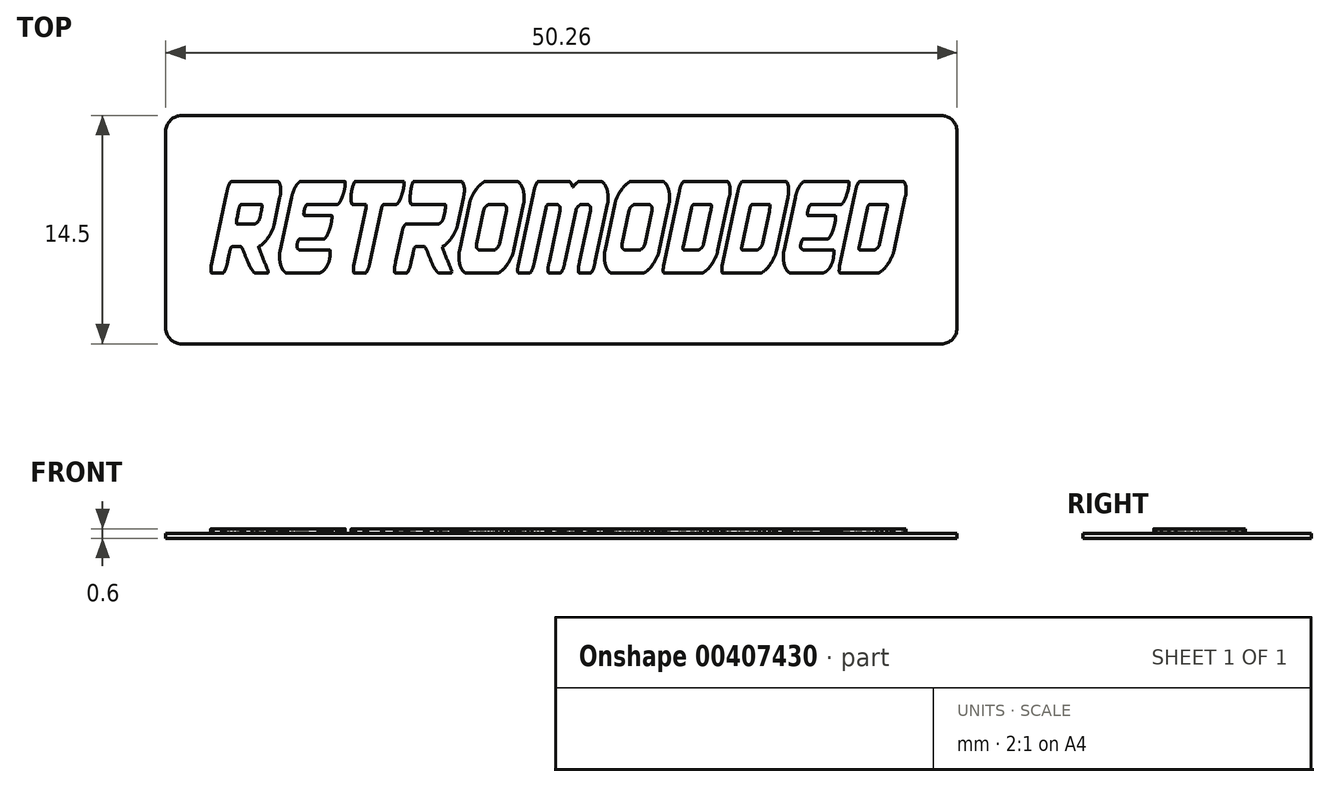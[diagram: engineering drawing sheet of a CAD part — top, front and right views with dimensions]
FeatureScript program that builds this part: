
annotation { "Feature Type Name" : "Feature", "Feature Type Description" : "" }
export const myFeature = defineFeature(function(context is Context, id is Id, definition is map)
    precondition{}
    {
        {
            var Q0;
            Q0=qCreatedBy(makeId("Top.planeOp"),FACE);
            var sketch = newSketch(context, id + "F0", { "sketchPlane" : qUnion([Q0])});
            skLineSegment(sketch, "E0.bottom", {"start": v(-24.13, 0) * mm, "end": v(24.13, 0) * mm});
            skLineSegment(sketch, "E0.top", {"start": v(-24.13, -14.5) * mm, "end": v(24.13, -14.5) * mm});
            skLineSegment(sketch, "E0.left", {"start": v(-25.12, -1) * mm, "end": v(-25.12, -13.5) * mm});
            skLineSegment(sketch, "E0.right", {"start": v(25.12, -1) * mm, "end": v(25.12, -13.5) * mm});
            skPoint(sketch, "E1.visualSharp", {"position": v(-25.13, 0) * mm});
            skArc(sketch, "E1.filletArc", {"start": v(-24.13, 0) * mm, "mid": v(-24.83, -0.3) * mm, "end": v(-25.13, -1) * mm});
            skPoint(sketch, "E2.visualSharp", {"position": v(-25.13, -14.5) * mm});
            skArc(sketch, "E2.filletArc", {"start": v(-25.13, -13.5) * mm, "mid": v(-24.83, -14.2) * mm, "end": v(-24.13, -14.5) * mm});
            skPoint(sketch, "E3.visualSharp", {"position": v(25.12, 0) * mm});
            skArc(sketch, "E3.filletArc", {"start": v(25.13, -1) * mm, "mid": v(24.83, -0.3) * mm, "end": v(24.13, 0) * mm});
            skPoint(sketch, "E4.visualSharp", {"position": v(25.12, -14.5) * mm});
            skArc(sketch, "E4.filletArc", {"start": v(24.13, -14.5) * mm, "mid": v(24.83, -14.2) * mm, "end": v(25.13, -13.5) * mm});
            skSolve(sketch);
        }
        {
            var Q0;
            Q0=qCreatedBy(makeId("Top.planeOp"),FACE);
            var sketch = newSketch(context, id + "F1", { "sketchPlane" : qUnion([Q0])});
            skLineSegment(sketch, "E5", {"start": v(-20.61, -6.53) * mm, "end": v(-20.5, -6.01) * mm});
            skFitSpline(sketch, "E6", {"points": [v(-20.5, -6.01) * mm, v(-20.48, -5.91) * mm, v(-20.45, -5.83) * mm, v(-20.42, -5.76) * mm]});
            skFitSpline(sketch, "E7", {"points": [v(-20.42, -5.76) * mm, v(-20.4, -5.69) * mm, v(-20.36, -5.65) * mm, v(-20.33, -5.64) * mm]});
            skLineSegment(sketch, "E8", {"start": v(-20.33, -5.64) * mm, "end": v(-19.09, -5.64) * mm});
            skFitSpline(sketch, "E9", {"points": [v(-19.09, -5.64) * mm, v(-19.04, -5.64) * mm, v(-19.02, -5.69) * mm, v(-19.02, -5.79) * mm]});
            skFitSpline(sketch, "E10", {"points": [v(-19.02, -5.79) * mm, v(-19.02, -5.83) * mm, v(-19.02, -5.88) * mm, v(-19.04, -5.95) * mm]});
            skFitSpline(sketch, "E11", {"points": [v(-19.04, -5.95) * mm, v(-19.04, -6) * mm, v(-19.05, -6.05) * mm, v(-19.06, -6.1) * mm]});
            skLineSegment(sketch, "E12", {"start": v(-19.06, -6.1) * mm, "end": v(-19.14, -6.49) * mm});
            skFitSpline(sketch, "E13", {"points": [v(-19.14, -6.49) * mm, v(-19.2, -6.62) * mm, v(-19.25, -6.72) * mm, v(-19.32, -6.79) * mm]});
            skFitSpline(sketch, "E14", {"points": [v(-19.32, -6.79) * mm, v(-19.4, -6.85) * mm, v(-19.46, -6.88) * mm, v(-19.53, -6.88) * mm]});
            skLineSegment(sketch, "E15", {"start": v(-19.53, -6.88) * mm, "end": v(-20.6, -6.88) * mm});
            skFitSpline(sketch, "E16", {"points": [v(-20.6, -6.88) * mm, v(-20.62, -6.88) * mm, v(-20.63, -6.83) * mm, v(-20.63, -6.74) * mm]});
            skFitSpline(sketch, "E17", {"points": [v(-20.63, -6.74) * mm, v(-20.63, -6.72) * mm, v(-20.63, -6.7) * mm, v(-20.63, -6.66) * mm]});
            skFitSpline(sketch, "E18", {"points": [v(-20.63, -6.66) * mm, v(-20.62, -6.62) * mm, v(-20.62, -6.58) * mm, v(-20.61, -6.53) * mm]});
            skLineSegment(sketch, "E19", {"start": v(-18.08, -4.18) * mm, "end": v(-20.86, -4.18) * mm});
            skFitSpline(sketch, "E20", {"points": [v(-20.86, -4.18) * mm, v(-20.96, -4.18) * mm, v(-21.03, -4.24) * mm, v(-21.09, -4.35) * mm]});
            skFitSpline(sketch, "E21", {"points": [v(-21.09, -4.35) * mm, v(-21.14, -4.46) * mm, v(-21.2, -4.64) * mm, v(-21.25, -4.9) * mm]});
            skLineSegment(sketch, "E22", {"start": v(-21.25, -4.9) * mm, "end": v(-22.19, -9.28) * mm});
            skFitSpline(sketch, "E23", {"points": [v(-22.19, -9.28) * mm, v(-22.2, -9.38) * mm, v(-22.22, -9.47) * mm, v(-22.24, -9.55) * mm]});
            skFitSpline(sketch, "E24", {"points": [v(-22.24, -9.55) * mm, v(-22.25, -9.63) * mm, v(-22.26, -9.7) * mm, v(-22.26, -9.76) * mm]});
            skFitSpline(sketch, "E25", {"points": [v(-22.26, -9.76) * mm, v(-22.26, -9.92) * mm, v(-22.2, -10) * mm, v(-22.1, -10) * mm]});
            skLineSegment(sketch, "E26", {"start": v(-22.1, -10) * mm, "end": v(-21.6, -10) * mm});
            skFitSpline(sketch, "E27", {"points": [v(-21.6, -10) * mm, v(-21.5, -10) * mm, v(-21.42, -9.94) * mm, v(-21.37, -9.82) * mm]});
            skFitSpline(sketch, "E28", {"points": [v(-21.37, -9.82) * mm, v(-21.3, -9.7) * mm, v(-21.25, -9.52) * mm, v(-21.2, -9.28) * mm]});
            skLineSegment(sketch, "E29", {"start": v(-21.2, -9.28) * mm, "end": v(-21.1, -8.79) * mm});
            skFitSpline(sketch, "E30", {"points": [v(-21.1, -8.79) * mm, v(-21.03, -8.5) * mm, v(-20.96, -8.35) * mm, v(-20.88, -8.33) * mm]});
            skLineSegment(sketch, "E31", {"start": v(-20.88, -8.33) * mm, "end": v(-20.35, -8.33) * mm});
            skFitSpline(sketch, "E32", {"points": [v(-20.35, -8.33) * mm, v(-20.27, -8.44) * mm, v(-20.2, -8.58) * mm, v(-20.13, -8.77) * mm]});
            skFitSpline(sketch, "E33", {"points": [v(-20.13, -8.77) * mm, v(-20.05, -8.96) * mm, v(-19.98, -9.14) * mm, v(-19.9, -9.33) * mm]});
            skFitSpline(sketch, "E34", {"points": [v(-19.9, -9.33) * mm, v(-19.82, -9.5) * mm, v(-19.73, -9.67) * mm, v(-19.64, -9.8) * mm]});
            skFitSpline(sketch, "E35", {"points": [v(-19.64, -9.8) * mm, v(-19.55, -9.93) * mm, v(-19.44, -10) * mm, v(-19.32, -10) * mm]});
            skLineSegment(sketch, "E36", {"start": v(-19.32, -10) * mm, "end": v(-18.66, -10) * mm});
            skFitSpline(sketch, "E37", {"points": [v(-18.66, -10) * mm, v(-18.65, -10) * mm, v(-18.64, -9.98) * mm, v(-18.62, -9.94) * mm]});
            skLineSegment(sketch, "E38", {"start": v(-18.62, -9.94) * mm, "end": v(-18.62, -9.9) * mm});
            skFitSpline(sketch, "E39", {"points": [v(-18.62, -9.9) * mm, v(-18.72, -9.63) * mm, v(-18.82, -9.37) * mm, v(-18.93, -9.13) * mm]});
            skFitSpline(sketch, "E40", {"points": [v(-18.93, -9.13) * mm, v(-19.03, -8.87) * mm, v(-19.13, -8.6) * mm, v(-19.24, -8.31) * mm]});
            skFitSpline(sketch, "E41", {"points": [v(-19.24, -8.31) * mm, v(-19.14, -8.28) * mm, v(-19.04, -8.22) * mm, v(-18.94, -8.12) * mm]});
            skFitSpline(sketch, "E42", {"points": [v(-18.94, -8.12) * mm, v(-18.84, -8.02) * mm, v(-18.74, -7.9) * mm, v(-18.65, -7.78) * mm]});
            skFitSpline(sketch, "E43", {"points": [v(-18.65, -7.78) * mm, v(-18.55, -7.64) * mm, v(-18.47, -7.5) * mm, v(-18.4, -7.35) * mm]});
            skFitSpline(sketch, "E44", {"points": [v(-18.4, -7.35) * mm, v(-18.33, -7.2) * mm, v(-18.28, -7.07) * mm, v(-18.25, -6.94) * mm]});
            skLineSegment(sketch, "E45", {"start": v(-18.25, -6.94) * mm, "end": v(-17.89, -5.2) * mm});
            skFitSpline(sketch, "E46", {"points": [v(-17.89, -5.2) * mm, v(-17.85, -5.04) * mm, v(-17.83, -4.88) * mm, v(-17.83, -4.73) * mm]});
            skFitSpline(sketch, "E47", {"points": [v(-17.83, -4.73) * mm, v(-17.83, -4.57) * mm, v(-17.85, -4.45) * mm, v(-17.9, -4.34) * mm]});
            skFitSpline(sketch, "E48", {"points": [v(-17.9, -4.34) * mm, v(-17.93, -4.24) * mm, v(-18, -4.18) * mm, v(-18.08, -4.18) * mm]});
            skFitSpline(sketch, "E49", {"points": [v(-17.86, -8.6) * mm, v(-17.89, -8.69) * mm, v(-17.9, -8.8) * mm, v(-17.9, -8.94) * mm]});
            skFitSpline(sketch, "E50", {"points": [v(-17.9, -8.94) * mm, v(-17.9, -9.07) * mm, v(-17.89, -9.2) * mm, v(-17.86, -9.32) * mm]});
            skFitSpline(sketch, "E51", {"points": [v(-17.86, -9.32) * mm, v(-17.84, -9.44) * mm, v(-17.8, -9.56) * mm, v(-17.76, -9.66) * mm]});
            skFitSpline(sketch, "E52", {"points": [v(-17.76, -9.66) * mm, v(-17.71, -9.76) * mm, v(-17.66, -9.84) * mm, v(-17.6, -9.9) * mm]});
            skFitSpline(sketch, "E53", {"points": [v(-17.6, -9.9) * mm, v(-17.53, -9.97) * mm, v(-17.46, -10) * mm, v(-17.38, -10) * mm]});
            skLineSegment(sketch, "E54", {"start": v(-17.38, -10) * mm, "end": v(-15.47, -10) * mm});
            skFitSpline(sketch, "E55", {"points": [v(-15.47, -10) * mm, v(-15.4, -10) * mm, v(-15.32, -9.98) * mm, v(-15.24, -9.94) * mm]});
            skFitSpline(sketch, "E56", {"points": [v(-15.24, -9.94) * mm, v(-15.16, -9.9) * mm, v(-15.1, -9.83) * mm, v(-15.02, -9.75) * mm]});
            skFitSpline(sketch, "E57", {"points": [v(-15.02, -9.75) * mm, v(-14.96, -9.67) * mm, v(-14.9, -9.58) * mm, v(-14.85, -9.47) * mm]});
            skFitSpline(sketch, "E58", {"points": [v(-14.85, -9.47) * mm, v(-14.8, -9.36) * mm, v(-14.75, -9.24) * mm, v(-14.72, -9.1) * mm]});
            skFitSpline(sketch, "E59", {"points": [v(-14.72, -9.1) * mm, v(-14.71, -9.07) * mm, v(-14.7, -9.02) * mm, v(-14.7, -8.93) * mm]});
            skFitSpline(sketch, "E60", {"points": [v(-14.7, -8.93) * mm, v(-14.69, -8.84) * mm, v(-14.68, -8.76) * mm, v(-14.68, -8.68) * mm]});
            skFitSpline(sketch, "E61", {"points": [v(-14.68, -8.68) * mm, v(-14.68, -8.59) * mm, v(-14.7, -8.54) * mm, v(-14.72, -8.54) * mm]});
            skLineSegment(sketch, "E62", {"start": v(-14.72, -8.54) * mm, "end": v(-16.55, -8.54) * mm});
            skFitSpline(sketch, "E63", {"points": [v(-16.55, -8.54) * mm, v(-16.6, -8.54) * mm, v(-16.66, -8.52) * mm, v(-16.72, -8.47) * mm]});
            skFitSpline(sketch, "E64", {"points": [v(-16.72, -8.47) * mm, v(-16.77, -8.43) * mm, v(-16.8, -8.35) * mm, v(-16.8, -8.25) * mm]});
            skFitSpline(sketch, "E65", {"points": [v(-16.8, -8.25) * mm, v(-16.8, -8.25) * mm, v(-16.8, -8.24) * mm, v(-16.8, -8.23) * mm]});
            skFitSpline(sketch, "E66", {"points": [v(-16.8, -8.23) * mm, v(-16.79, -8.2) * mm, v(-16.79, -8.19) * mm, v(-16.78, -8.16) * mm]});
            skFitSpline(sketch, "E67", {"points": [v(-16.78, -8.16) * mm, v(-16.75, -8.05) * mm, v(-16.72, -7.96) * mm, v(-16.7, -7.91) * mm]});
            skFitSpline(sketch, "E68", {"points": [v(-16.7, -7.91) * mm, v(-16.67, -7.86) * mm, v(-16.63, -7.83) * mm, v(-16.58, -7.83) * mm]});
            skLineSegment(sketch, "E69", {"start": v(-16.58, -7.83) * mm, "end": v(-15.1, -7.83) * mm});
            skFitSpline(sketch, "E70", {"points": [v(-15.1, -7.83) * mm, v(-15.05, -7.83) * mm, v(-15, -7.8) * mm, v(-14.96, -7.74) * mm]});
            skFitSpline(sketch, "E71", {"points": [v(-14.96, -7.74) * mm, v(-14.92, -7.67) * mm, v(-14.87, -7.6) * mm, v(-14.83, -7.5) * mm]});
            skFitSpline(sketch, "E72", {"points": [v(-14.83, -7.5) * mm, v(-14.79, -7.4) * mm, v(-14.75, -7.3) * mm, v(-14.71, -7.18) * mm]});
            skFitSpline(sketch, "E73", {"points": [v(-14.71, -7.18) * mm, v(-14.68, -7.07) * mm, v(-14.65, -6.96) * mm, v(-14.62, -6.86) * mm]});
            skFitSpline(sketch, "E74", {"points": [v(-14.62, -6.86) * mm, v(-14.61, -6.83) * mm, v(-14.6, -6.77) * mm, v(-14.6, -6.7) * mm]});
            skFitSpline(sketch, "E75", {"points": [v(-14.6, -6.7) * mm, v(-14.58, -6.6) * mm, v(-14.58, -6.53) * mm, v(-14.58, -6.47) * mm]});
            skFitSpline(sketch, "E76", {"points": [v(-14.58, -6.47) * mm, v(-14.58, -6.4) * mm, v(-14.59, -6.35) * mm, v(-14.61, -6.35) * mm]});
            skLineSegment(sketch, "E77", {"start": v(-14.61, -6.35) * mm, "end": v(-16.3, -6.35) * mm});
            skFitSpline(sketch, "E78", {"points": [v(-16.3, -6.35) * mm, v(-16.32, -6.35) * mm, v(-16.34, -6.34) * mm, v(-16.35, -6.31) * mm]});
            skFitSpline(sketch, "E79", {"points": [v(-16.35, -6.31) * mm, v(-16.35, -6.28) * mm, v(-16.36, -6.25) * mm, v(-16.36, -6.22) * mm]});
            skFitSpline(sketch, "E80", {"points": [v(-16.36, -6.22) * mm, v(-16.36, -6.2) * mm, v(-16.36, -6.2) * mm, v(-16.36, -6.18) * mm]});
            skFitSpline(sketch, "E81", {"points": [v(-16.36, -6.18) * mm, v(-16.35, -6.16) * mm, v(-16.35, -6.14) * mm, v(-16.35, -6.1) * mm]});
            skFitSpline(sketch, "E82", {"points": [v(-16.35, -6.1) * mm, v(-16.34, -6.06) * mm, v(-16.33, -6.01) * mm, v(-16.32, -5.96) * mm]});
            skFitSpline(sketch, "E83", {"points": [v(-16.32, -5.96) * mm, v(-16.3, -5.9) * mm, v(-16.28, -5.86) * mm, v(-16.26, -5.81) * mm]});
            skFitSpline(sketch, "E84", {"points": [v(-16.26, -5.81) * mm, v(-16.24, -5.76) * mm, v(-16.22, -5.72) * mm, v(-16.2, -5.7) * mm]});
            skFitSpline(sketch, "E85", {"points": [v(-16.2, -5.7) * mm, v(-16.17, -5.66) * mm, v(-16.15, -5.64) * mm, v(-16.12, -5.64) * mm]});
            skLineSegment(sketch, "E86", {"start": v(-16.12, -5.64) * mm, "end": v(-14.26, -5.64) * mm});
            skFitSpline(sketch, "E87", {"points": [v(-14.26, -5.64) * mm, v(-14.22, -5.64) * mm, v(-14.17, -5.61) * mm, v(-14.12, -5.56) * mm]});
            skFitSpline(sketch, "E88", {"points": [v(-14.12, -5.56) * mm, v(-14.07, -5.5) * mm, v(-14.03, -5.42) * mm, v(-13.99, -5.33) * mm]});
            skFitSpline(sketch, "E89", {"points": [v(-13.99, -5.33) * mm, v(-13.94, -5.23) * mm, v(-13.9, -5.13) * mm, v(-13.87, -5.01) * mm]});
            skFitSpline(sketch, "E90", {"points": [v(-13.87, -5.01) * mm, v(-13.83, -4.9) * mm, v(-13.8, -4.8) * mm, v(-13.77, -4.7) * mm]});
            skFitSpline(sketch, "E91", {"points": [v(-13.77, -4.7) * mm, v(-13.76, -4.66) * mm, v(-13.76, -4.6) * mm, v(-13.74, -4.52) * mm]});
            skFitSpline(sketch, "E92", {"points": [v(-13.74, -4.52) * mm, v(-13.73, -4.44) * mm, v(-13.73, -4.36) * mm, v(-13.73, -4.3) * mm]});
            skFitSpline(sketch, "E93", {"points": [v(-13.73, -4.3) * mm, v(-13.73, -4.22) * mm, v(-13.74, -4.18) * mm, v(-13.77, -4.18) * mm]});
            skLineSegment(sketch, "E94", {"start": v(-13.77, -4.18) * mm, "end": v(-16.5, -4.18) * mm});
            skFitSpline(sketch, "E95", {"points": [v(-16.5, -4.18) * mm, v(-16.57, -4.18) * mm, v(-16.64, -4.21) * mm, v(-16.7, -4.28) * mm]});
            skFitSpline(sketch, "E96", {"points": [v(-16.7, -4.28) * mm, v(-16.76, -4.33) * mm, v(-16.82, -4.4) * mm, v(-16.88, -4.5) * mm]});
            skFitSpline(sketch, "E97", {"points": [v(-16.88, -4.5) * mm, v(-16.93, -4.6) * mm, v(-16.98, -4.71) * mm, v(-17.03, -4.84) * mm]});
            skFitSpline(sketch, "E98", {"points": [v(-17.03, -4.84) * mm, v(-17.07, -4.96) * mm, v(-17.1, -5.08) * mm, v(-17.14, -5.2) * mm]});
            skLineSegment(sketch, "E99", {"start": v(-17.14, -5.2) * mm, "end": v(-17.86, -8.6) * mm});
            skFitSpline(sketch, "E100", {"points": [v(-13.14, -9.28) * mm, v(-13.16, -9.38) * mm, v(-13.17, -9.47) * mm, v(-13.19, -9.55) * mm]});
            skFitSpline(sketch, "E101", {"points": [v(-13.19, -9.55) * mm, v(-13.2, -9.63) * mm, v(-13.2, -9.7) * mm, v(-13.2, -9.76) * mm]});
            skFitSpline(sketch, "E102", {"points": [v(-13.2, -9.76) * mm, v(-13.2, -9.92) * mm, v(-13.16, -10) * mm, v(-13.06, -10) * mm]});
            skLineSegment(sketch, "E103", {"start": v(-13.06, -10) * mm, "end": v(-12.54, -10) * mm});
            skFitSpline(sketch, "E104", {"points": [v(-12.54, -10) * mm, v(-12.45, -10) * mm, v(-12.37, -9.94) * mm, v(-12.32, -9.82) * mm]});
            skFitSpline(sketch, "E105", {"points": [v(-12.32, -9.82) * mm, v(-12.26, -9.7) * mm, v(-12.2, -9.52) * mm, v(-12.15, -9.28) * mm]});
            skLineSegment(sketch, "E106", {"start": v(-12.15, -9.28) * mm, "end": v(-11.43, -5.89) * mm});
            skFitSpline(sketch, "E107", {"points": [v(-11.43, -5.89) * mm, v(-11.4, -5.82) * mm, v(-11.38, -5.77) * mm, v(-11.35, -5.72) * mm]});
            skFitSpline(sketch, "E108", {"points": [v(-11.35, -5.72) * mm, v(-11.32, -5.67) * mm, v(-11.3, -5.64) * mm, v(-11.28, -5.64) * mm]});
            skLineSegment(sketch, "E109", {"start": v(-11.28, -5.64) * mm, "end": v(-10.52, -5.64) * mm});
            skFitSpline(sketch, "E110", {"points": [v(-10.52, -5.64) * mm, v(-10.48, -5.64) * mm, v(-10.43, -5.61) * mm, v(-10.38, -5.56) * mm]});
            skFitSpline(sketch, "E111", {"points": [v(-10.38, -5.56) * mm, v(-10.33, -5.5) * mm, v(-10.29, -5.42) * mm, v(-10.25, -5.33) * mm]});
            skFitSpline(sketch, "E112", {"points": [v(-10.25, -5.33) * mm, v(-10.2, -5.23) * mm, v(-10.16, -5.13) * mm, v(-10.13, -5.01) * mm]});
            skFitSpline(sketch, "E113", {"points": [v(-10.13, -5.01) * mm, v(-10.1, -4.9) * mm, v(-10.06, -4.8) * mm, v(-10.04, -4.7) * mm]});
            skFitSpline(sketch, "E114", {"points": [v(-10.04, -4.7) * mm, v(-10.03, -4.66) * mm, v(-10.02, -4.6) * mm, v(-10, -4.52) * mm]});
            skFitSpline(sketch, "E115", {"points": [v(-10, -4.52) * mm, v(-10, -4.44) * mm, v(-10, -4.36) * mm, v(-10, -4.3) * mm]});
            skFitSpline(sketch, "E116", {"points": [v(-10, -4.3) * mm, v(-10, -4.22) * mm, v(-10, -4.18) * mm, v(-10.03, -4.18) * mm]});
            skLineSegment(sketch, "E117", {"start": v(-10.03, -4.18) * mm, "end": v(-13.08, -4.18) * mm});
            skFitSpline(sketch, "E118", {"points": [v(-13.08, -4.18) * mm, v(-13.1, -4.18) * mm, v(-13.12, -4.2) * mm, v(-13.15, -4.25) * mm]});
            skFitSpline(sketch, "E119", {"points": [v(-13.15, -4.25) * mm, v(-13.17, -4.3) * mm, v(-13.2, -4.34) * mm, v(-13.21, -4.4) * mm]});
            skFitSpline(sketch, "E120", {"points": [v(-13.21, -4.4) * mm, v(-13.23, -4.45) * mm, v(-13.25, -4.5) * mm, v(-13.27, -4.56) * mm]});
            skFitSpline(sketch, "E121", {"points": [v(-13.27, -4.56) * mm, v(-13.28, -4.61) * mm, v(-13.3, -4.66) * mm, v(-13.3, -4.68) * mm]});
            skFitSpline(sketch, "E122", {"points": [v(-13.3, -4.68) * mm, v(-13.32, -4.78) * mm, v(-13.34, -4.88) * mm, v(-13.34, -4.97) * mm]});
            skFitSpline(sketch, "E123", {"points": [v(-13.34, -4.97) * mm, v(-13.35, -5.06) * mm, v(-13.35, -5.15) * mm, v(-13.35, -5.24) * mm]});
            skFitSpline(sketch, "E124", {"points": [v(-13.35, -5.24) * mm, v(-13.35, -5.36) * mm, v(-13.35, -5.45) * mm, v(-13.33, -5.53) * mm]});
            skFitSpline(sketch, "E125", {"points": [v(-13.33, -5.53) * mm, v(-13.3, -5.6) * mm, v(-13.27, -5.64) * mm, v(-13.21, -5.64) * mm]});
            skLineSegment(sketch, "E126", {"start": v(-13.21, -5.64) * mm, "end": v(-12.46, -5.64) * mm});
            skFitSpline(sketch, "E127", {"points": [v(-12.46, -5.64) * mm, v(-12.42, -5.64) * mm, v(-12.4, -5.7) * mm, v(-12.4, -5.8) * mm]});
            skFitSpline(sketch, "E128", {"points": [v(-12.4, -5.8) * mm, v(-12.4, -5.8) * mm, v(-12.4, -5.81) * mm, v(-12.41, -5.83) * mm]});
            skFitSpline(sketch, "E129", {"points": [v(-12.41, -5.83) * mm, v(-12.41, -5.84) * mm, v(-12.41, -5.86) * mm, v(-12.42, -5.89) * mm]});
            skLineSegment(sketch, "E130", {"start": v(-12.42, -5.89) * mm, "end": v(-13.14, -9.28) * mm});
            skLineSegment(sketch, "E131", {"start": v(-13.14, -9.28) * mm, "end": v(-13.14, -9.28) * mm});
            skLineSegment(sketch, "E132", {"start": v(-7.43, -5.64) * mm, "end": v(-9.47, -5.64) * mm});
            skFitSpline(sketch, "E133", {"points": [v(-9.47, -5.64) * mm, v(-9.52, -5.64) * mm, v(-9.56, -5.6) * mm, v(-9.58, -5.53) * mm]});
            skFitSpline(sketch, "E134", {"points": [v(-9.58, -5.53) * mm, v(-9.6, -5.45) * mm, v(-9.6, -5.36) * mm, v(-9.6, -5.24) * mm]});
            skFitSpline(sketch, "E135", {"points": [v(-9.6, -5.24) * mm, v(-9.6, -5.2) * mm, v(-9.6, -5.1) * mm, v(-9.6, -5) * mm]});
            skFitSpline(sketch, "E136", {"points": [v(-9.6, -5) * mm, v(-9.58, -4.88) * mm, v(-9.56, -4.76) * mm, v(-9.54, -4.64) * mm]});
            skFitSpline(sketch, "E137", {"points": [v(-9.54, -4.64) * mm, v(-9.52, -4.52) * mm, v(-9.5, -4.42) * mm, v(-9.46, -4.33) * mm]});
            skFitSpline(sketch, "E138", {"points": [v(-9.46, -4.33) * mm, v(-9.43, -4.23) * mm, v(-9.39, -4.18) * mm, v(-9.34, -4.18) * mm]});
            skLineSegment(sketch, "E139", {"start": v(-9.34, -4.18) * mm, "end": v(-6.42, -4.18) * mm});
            skFitSpline(sketch, "E140", {"points": [v(-6.42, -4.18) * mm, v(-6.33, -4.18) * mm, v(-6.27, -4.24) * mm, v(-6.23, -4.34) * mm]});
            skFitSpline(sketch, "E141", {"points": [v(-6.23, -4.34) * mm, v(-6.19, -4.45) * mm, v(-6.16, -4.57) * mm, v(-6.16, -4.73) * mm]});
            skFitSpline(sketch, "E142", {"points": [v(-6.16, -4.73) * mm, v(-6.16, -4.88) * mm, v(-6.18, -5.04) * mm, v(-6.22, -5.2) * mm]});
            skLineSegment(sketch, "E143", {"start": v(-6.22, -5.2) * mm, "end": v(-6.59, -6.94) * mm});
            skFitSpline(sketch, "E144", {"points": [v(-6.59, -6.94) * mm, v(-6.62, -7.07) * mm, v(-6.67, -7.2) * mm, v(-6.74, -7.35) * mm]});
            skFitSpline(sketch, "E145", {"points": [v(-6.74, -7.35) * mm, v(-6.8, -7.5) * mm, v(-6.89, -7.64) * mm, v(-6.98, -7.78) * mm]});
            skFitSpline(sketch, "E146", {"points": [v(-6.98, -7.78) * mm, v(-7.07, -7.9) * mm, v(-7.17, -8.02) * mm, v(-7.28, -8.12) * mm]});
            skFitSpline(sketch, "E147", {"points": [v(-7.28, -8.12) * mm, v(-7.38, -8.22) * mm, v(-7.48, -8.28) * mm, v(-7.57, -8.31) * mm]});
            skFitSpline(sketch, "E148", {"points": [v(-7.57, -8.31) * mm, v(-7.47, -8.6) * mm, v(-7.37, -8.87) * mm, v(-7.27, -9.13) * mm]});
            skFitSpline(sketch, "E149", {"points": [v(-7.27, -9.13) * mm, v(-7.16, -9.37) * mm, v(-7.06, -9.63) * mm, v(-6.95, -9.9) * mm]});
            skLineSegment(sketch, "E150", {"start": v(-6.95, -9.9) * mm, "end": v(-6.96, -9.94) * mm});
            skFitSpline(sketch, "E151", {"points": [v(-6.96, -9.94) * mm, v(-6.98, -9.98) * mm, v(-6.99, -10) * mm, v(-7, -10) * mm]});
            skLineSegment(sketch, "E152", {"start": v(-7, -10) * mm, "end": v(-7.66, -10) * mm});
            skFitSpline(sketch, "E153", {"points": [v(-7.66, -10) * mm, v(-7.78, -10) * mm, v(-7.89, -9.93) * mm, v(-7.98, -9.8) * mm]});
            skFitSpline(sketch, "E154", {"points": [v(-7.98, -9.8) * mm, v(-8.07, -9.67) * mm, v(-8.16, -9.5) * mm, v(-8.23, -9.33) * mm]});
            skFitSpline(sketch, "E155", {"points": [v(-8.23, -9.33) * mm, v(-8.31, -9.14) * mm, v(-8.4, -8.96) * mm, v(-8.46, -8.77) * mm]});
            skFitSpline(sketch, "E156", {"points": [v(-8.46, -8.77) * mm, v(-8.54, -8.58) * mm, v(-8.6, -8.44) * mm, v(-8.68, -8.33) * mm]});
            skLineSegment(sketch, "E157", {"start": v(-8.68, -8.33) * mm, "end": v(-9.21, -8.33) * mm});
            skFitSpline(sketch, "E158", {"points": [v(-9.21, -8.33) * mm, v(-9.3, -8.35) * mm, v(-9.37, -8.5) * mm, v(-9.43, -8.79) * mm]});
            skLineSegment(sketch, "E159", {"start": v(-9.43, -8.79) * mm, "end": v(-9.53, -9.28) * mm});
            skFitSpline(sketch, "E160", {"points": [v(-9.53, -9.28) * mm, v(-9.59, -9.52) * mm, v(-9.65, -9.7) * mm, v(-9.7, -9.82) * mm]});
            skFitSpline(sketch, "E161", {"points": [v(-9.7, -9.82) * mm, v(-9.76, -9.94) * mm, v(-9.83, -10) * mm, v(-9.93, -10) * mm]});
            skLineSegment(sketch, "E162", {"start": v(-9.93, -10) * mm, "end": v(-10.45, -10) * mm});
            skFitSpline(sketch, "E163", {"points": [v(-10.45, -10) * mm, v(-10.55, -10) * mm, v(-10.6, -9.92) * mm, v(-10.6, -9.76) * mm]});
            skFitSpline(sketch, "E164", {"points": [v(-10.6, -9.76) * mm, v(-10.6, -9.7) * mm, v(-10.59, -9.63) * mm, v(-10.58, -9.55) * mm]});
            skFitSpline(sketch, "E165", {"points": [v(-10.58, -9.55) * mm, v(-10.56, -9.47) * mm, v(-10.54, -9.38) * mm, v(-10.52, -9.28) * mm]});
            skLineSegment(sketch, "E166", {"start": v(-10.52, -9.28) * mm, "end": v(-10.12, -7.39) * mm});
            skFitSpline(sketch, "E167", {"points": [v(-10.12, -7.39) * mm, v(-10.08, -7.2) * mm, v(-10.03, -7.08) * mm, v(-9.98, -7) * mm]});
            skFitSpline(sketch, "E168", {"points": [v(-9.98, -7) * mm, v(-9.92, -6.92) * mm, v(-9.86, -6.88) * mm, v(-9.78, -6.88) * mm]});
            skLineSegment(sketch, "E169", {"start": v(-9.78, -6.88) * mm, "end": v(-7.86, -6.88) * mm});
            skFitSpline(sketch, "E170", {"points": [v(-7.86, -6.88) * mm, v(-7.8, -6.88) * mm, v(-7.73, -6.85) * mm, v(-7.66, -6.79) * mm]});
            skFitSpline(sketch, "E171", {"points": [v(-7.66, -6.79) * mm, v(-7.6, -6.72) * mm, v(-7.53, -6.62) * mm, v(-7.48, -6.49) * mm]});
            skLineSegment(sketch, "E172", {"start": v(-7.48, -6.49) * mm, "end": v(-7.4, -6.1) * mm});
            skFitSpline(sketch, "E173", {"points": [v(-7.4, -6.1) * mm, v(-7.39, -6.05) * mm, v(-7.38, -6) * mm, v(-7.37, -5.95) * mm]});
            skFitSpline(sketch, "E174", {"points": [v(-7.37, -5.95) * mm, v(-7.36, -5.88) * mm, v(-7.36, -5.83) * mm, v(-7.36, -5.79) * mm]});
            skFitSpline(sketch, "E175", {"points": [v(-7.36, -5.79) * mm, v(-7.36, -5.69) * mm, v(-7.38, -5.64) * mm, v(-7.43, -5.64) * mm]});
            skFitSpline(sketch, "E176", {"points": [v(-2.4, -5.57) * mm, v(-2.37, -5.51) * mm, v(-2.36, -5.4) * mm, v(-2.36, -5.24) * mm]});
            skFitSpline(sketch, "E177", {"points": [v(-2.36, -5.24) * mm, v(-2.36, -5.12) * mm, v(-2.38, -5) * mm, v(-2.4, -4.87) * mm]});
            skFitSpline(sketch, "E178", {"points": [v(-2.4, -4.87) * mm, v(-2.42, -4.74) * mm, v(-2.46, -4.62) * mm, v(-2.5, -4.52) * mm]});
            skFitSpline(sketch, "E179", {"points": [v(-2.5, -4.52) * mm, v(-2.55, -4.42) * mm, v(-2.6, -4.34) * mm, v(-2.66, -4.28) * mm]});
            skFitSpline(sketch, "E180", {"points": [v(-2.66, -4.28) * mm, v(-2.73, -4.21) * mm, v(-2.8, -4.18) * mm, v(-2.88, -4.18) * mm]});
            skLineSegment(sketch, "E181", {"start": v(-2.88, -4.18) * mm, "end": v(-4.75, -4.18) * mm});
            skFitSpline(sketch, "E182", {"points": [v(-4.75, -4.18) * mm, v(-4.85, -4.18) * mm, v(-4.95, -4.23) * mm, v(-5.07, -4.33) * mm]});
            skFitSpline(sketch, "E183", {"points": [v(-5.07, -4.33) * mm, v(-5.18, -4.42) * mm, v(-5.29, -4.53) * mm, v(-5.4, -4.67) * mm]});
            skFitSpline(sketch, "E184", {"points": [v(-5.4, -4.67) * mm, v(-5.5, -4.81) * mm, v(-5.6, -4.96) * mm, v(-5.67, -5.12) * mm]});
            skFitSpline(sketch, "E185", {"points": [v(-5.67, -5.12) * mm, v(-5.75, -5.29) * mm, v(-5.8, -5.44) * mm, v(-5.83, -5.57) * mm]});
            skLineSegment(sketch, "E186", {"start": v(-5.83, -5.57) * mm, "end": v(-6.48, -8.6) * mm});
            skFitSpline(sketch, "E187", {"points": [v(-6.48, -8.6) * mm, v(-6.5, -8.69) * mm, v(-6.51, -8.8) * mm, v(-6.51, -8.94) * mm]});
            skFitSpline(sketch, "E188", {"points": [v(-6.51, -8.94) * mm, v(-6.51, -9.07) * mm, v(-6.5, -9.2) * mm, v(-6.48, -9.32) * mm]});
            skFitSpline(sketch, "E189", {"points": [v(-6.48, -9.32) * mm, v(-6.45, -9.44) * mm, v(-6.42, -9.56) * mm, v(-6.38, -9.66) * mm]});
            skFitSpline(sketch, "E190", {"points": [v(-6.38, -9.66) * mm, v(-6.33, -9.76) * mm, v(-6.27, -9.84) * mm, v(-6.21, -9.9) * mm]});
            skFitSpline(sketch, "E191", {"points": [v(-6.21, -9.9) * mm, v(-6.14, -9.97) * mm, v(-6.07, -10) * mm, v(-6, -10) * mm]});
            skLineSegment(sketch, "E192", {"start": v(-6, -10) * mm, "end": v(-4.12, -10) * mm});
            skFitSpline(sketch, "E193", {"points": [v(-4.12, -10) * mm, v(-4.02, -10) * mm, v(-3.92, -9.95) * mm, v(-3.8, -9.86) * mm]});
            skFitSpline(sketch, "E194", {"points": [v(-3.8, -9.86) * mm, v(-3.69, -9.77) * mm, v(-3.58, -9.65) * mm, v(-3.48, -9.52) * mm]});
            skFitSpline(sketch, "E195", {"points": [v(-3.48, -9.52) * mm, v(-3.38, -9.37) * mm, v(-3.29, -9.22) * mm, v(-3.2, -9.06) * mm]});
            skFitSpline(sketch, "E196", {"points": [v(-3.2, -9.06) * mm, v(-3.12, -8.9) * mm, v(-3.07, -8.74) * mm, v(-3.04, -8.6) * mm]});
            skLineSegment(sketch, "E197", {"start": v(-3.04, -8.6) * mm, "end": v(-2.4, -5.57) * mm});
            skFitSpline(sketch, "E198", {"points": [v(-3.73, -5.64) * mm, v(-3.67, -5.64) * mm, v(-3.6, -5.67) * mm, v(-3.56, -5.73) * mm]});
            skFitSpline(sketch, "E199", {"points": [v(-3.56, -5.73) * mm, v(-3.5, -5.78) * mm, v(-3.48, -5.87) * mm, v(-3.48, -5.99) * mm]});
            skLineSegment(sketch, "E200", {"start": v(-3.48, -5.99) * mm, "end": v(-3.48, -6.02) * mm});
            skLineSegment(sketch, "E201", {"start": v(-3.48, -6.02) * mm, "end": v(-3.94, -8.16) * mm});
            skFitSpline(sketch, "E202", {"points": [v(-3.94, -8.16) * mm, v(-3.99, -8.28) * mm, v(-4.05, -8.38) * mm, v(-4.12, -8.45) * mm]});
            skFitSpline(sketch, "E203", {"points": [v(-4.12, -8.45) * mm, v(-4.2, -8.5) * mm, v(-4.27, -8.54) * mm, v(-4.33, -8.54) * mm]});
            skLineSegment(sketch, "E204", {"start": v(-4.33, -8.54) * mm, "end": v(-5.15, -8.54) * mm});
            skFitSpline(sketch, "E205", {"points": [v(-5.15, -8.54) * mm, v(-5.21, -8.54) * mm, v(-5.27, -8.51) * mm, v(-5.32, -8.46) * mm]});
            skFitSpline(sketch, "E206", {"points": [v(-5.32, -8.46) * mm, v(-5.37, -8.4) * mm, v(-5.4, -8.31) * mm, v(-5.4, -8.2) * mm]});
            skLineSegment(sketch, "E207", {"start": v(-5.4, -8.2) * mm, "end": v(-5.4, -8.16) * mm});
            skLineSegment(sketch, "E208", {"start": v(-5.4, -8.16) * mm, "end": v(-4.94, -6.02) * mm});
            skFitSpline(sketch, "E209", {"points": [v(-4.94, -6.02) * mm, v(-4.89, -5.9) * mm, v(-4.83, -5.8) * mm, v(-4.75, -5.73) * mm]});
            skFitSpline(sketch, "E210", {"points": [v(-4.75, -5.73) * mm, v(-4.66, -5.67) * mm, v(-4.6, -5.64) * mm, v(-4.53, -5.64) * mm]});
            skLineSegment(sketch, "E211", {"start": v(-4.53, -5.64) * mm, "end": v(-3.73, -5.64) * mm});
            skLineSegment(sketch, "E212", {"start": v(-1.7, -9.28) * mm, "end": v(-0.99, -5.89) * mm});
            skFitSpline(sketch, "E213", {"points": [v(-0.99, -5.89) * mm, v(-0.98, -5.83) * mm, v(-0.96, -5.78) * mm, v(-0.93, -5.73) * mm]});
            skFitSpline(sketch, "E214", {"points": [v(-0.93, -5.73) * mm, v(-0.9, -5.67) * mm, v(-0.87, -5.64) * mm, v(-0.84, -5.64) * mm]});
            skLineSegment(sketch, "E215", {"start": v(-0.84, -5.64) * mm, "end": v(-0.33, -5.64) * mm});
            skFitSpline(sketch, "E216", {"points": [v(-0.33, -5.64) * mm, v(-0.26, -5.64) * mm, v(-0.2, -5.67) * mm, v(-0.15, -5.73) * mm]});
            skFitSpline(sketch, "E217", {"points": [v(-0.15, -5.73) * mm, v(-0.1, -5.78) * mm, v(-0.07, -5.87) * mm, v(-0.07, -5.99) * mm]});
            skLineSegment(sketch, "E218", {"start": v(-0.07, -5.99) * mm, "end": v(-0.07, -6.02) * mm});
            skLineSegment(sketch, "E219", {"start": v(-0.07, -6.02) * mm, "end": v(-0.76, -9.28) * mm});
            skFitSpline(sketch, "E220", {"points": [v(-0.76, -9.28) * mm, v(-0.82, -9.48) * mm, v(-0.84, -9.64) * mm, v(-0.84, -9.78) * mm]});
            skFitSpline(sketch, "E221", {"points": [v(-0.84, -9.78) * mm, v(-0.84, -9.92) * mm, v(-0.79, -10) * mm, v(-0.69, -10) * mm]});
            skLineSegment(sketch, "E222", {"start": v(-0.69, -10) * mm, "end": v(-0.17, -10) * mm});
            skFitSpline(sketch, "E223", {"points": [v(-0.17, -10) * mm, v(-0.07, -10) * mm, v(0, -9.94) * mm, v(0.06, -9.84) * mm]});
            skFitSpline(sketch, "E224", {"points": [v(0.06, -9.84) * mm, v(0.12, -9.72) * mm, v(0.17, -9.54) * mm, v(0.23, -9.28) * mm]});
            skLineSegment(sketch, "E225", {"start": v(0.23, -9.28) * mm, "end": v(0.92, -6.02) * mm});
            skFitSpline(sketch, "E226", {"points": [v(0.92, -6.02) * mm, v(0.96, -5.9) * mm, v(1.03, -5.8) * mm, v(1.1, -5.74) * mm]});
            skFitSpline(sketch, "E227", {"points": [v(1.1, -5.74) * mm, v(1.18, -5.68) * mm, v(1.25, -5.64) * mm, v(1.31, -5.64) * mm]});
            skLineSegment(sketch, "E228", {"start": v(1.31, -5.64) * mm, "end": v(1.6, -5.64) * mm});
            skFitSpline(sketch, "E229", {"points": [v(1.6, -5.64) * mm, v(1.67, -5.64) * mm, v(1.73, -5.67) * mm, v(1.78, -5.73) * mm]});
            skFitSpline(sketch, "E230", {"points": [v(1.78, -5.73) * mm, v(1.84, -5.78) * mm, v(1.86, -5.87) * mm, v(1.86, -5.99) * mm]});
            skLineSegment(sketch, "E231", {"start": v(1.86, -5.99) * mm, "end": v(1.86, -6.02) * mm});
            skLineSegment(sketch, "E232", {"start": v(1.86, -6.02) * mm, "end": v(1.17, -9.28) * mm});
            skFitSpline(sketch, "E233", {"points": [v(1.17, -9.28) * mm, v(1.11, -9.48) * mm, v(1.09, -9.64) * mm, v(1.09, -9.78) * mm]});
            skFitSpline(sketch, "E234", {"points": [v(1.09, -9.78) * mm, v(1.09, -9.92) * mm, v(1.14, -10) * mm, v(1.24, -10) * mm]});
            skLineSegment(sketch, "E235", {"start": v(1.24, -10) * mm, "end": v(1.76, -10) * mm});
            skFitSpline(sketch, "E236", {"points": [v(1.76, -10) * mm, v(1.85, -10) * mm, v(1.92, -9.94) * mm, v(1.98, -9.84) * mm]});
            skFitSpline(sketch, "E237", {"points": [v(1.98, -9.84) * mm, v(2.04, -9.72) * mm, v(2.1, -9.54) * mm, v(2.15, -9.28) * mm]});
            skLineSegment(sketch, "E238", {"start": v(2.15, -9.28) * mm, "end": v(2.94, -5.57) * mm});
            skFitSpline(sketch, "E239", {"points": [v(2.94, -5.57) * mm, v(2.96, -5.51) * mm, v(2.97, -5.4) * mm, v(2.97, -5.24) * mm]});
            skFitSpline(sketch, "E240", {"points": [v(2.97, -5.24) * mm, v(2.97, -5.12) * mm, v(2.96, -5) * mm, v(2.94, -4.87) * mm]});
            skFitSpline(sketch, "E241", {"points": [v(2.94, -4.87) * mm, v(2.91, -4.74) * mm, v(2.88, -4.62) * mm, v(2.83, -4.52) * mm]});
            skFitSpline(sketch, "E242", {"points": [v(2.83, -4.52) * mm, v(2.79, -4.42) * mm, v(2.73, -4.34) * mm, v(2.67, -4.28) * mm]});
            skFitSpline(sketch, "E243", {"points": [v(2.67, -4.28) * mm, v(2.6, -4.21) * mm, v(2.53, -4.18) * mm, v(2.45, -4.18) * mm]});
            skLineSegment(sketch, "E244", {"start": v(2.45, -4.18) * mm, "end": v(1.2, -4.18) * mm});
            skFitSpline(sketch, "E245", {"points": [v(1.2, -4.18) * mm, v(1.12, -4.18) * mm, v(1.04, -4.22) * mm, v(0.97, -4.28) * mm]});
            skFitSpline(sketch, "E246", {"points": [v(0.97, -4.28) * mm, v(0.9, -4.35) * mm, v(0.82, -4.43) * mm, v(0.73, -4.54) * mm]});
            skFitSpline(sketch, "E247", {"points": [v(0.73, -4.54) * mm, v(0.69, -4.43) * mm, v(0.64, -4.35) * mm, v(0.6, -4.28) * mm]});
            skFitSpline(sketch, "E248", {"points": [v(0.6, -4.28) * mm, v(0.56, -4.22) * mm, v(0.5, -4.18) * mm, v(0.4, -4.18) * mm]});
            skLineSegment(sketch, "E249", {"start": v(0.4, -4.18) * mm, "end": v(-1.38, -4.18) * mm});
            skFitSpline(sketch, "E250", {"points": [v(-1.38, -4.18) * mm, v(-1.47, -4.18) * mm, v(-1.54, -4.24) * mm, v(-1.6, -4.36) * mm]});
            skFitSpline(sketch, "E251", {"points": [v(-1.6, -4.36) * mm, v(-1.66, -4.48) * mm, v(-1.71, -4.66) * mm, v(-1.77, -4.9) * mm]});
            skLineSegment(sketch, "E252", {"start": v(-1.77, -4.9) * mm, "end": v(-2.7, -9.28) * mm});
            skFitSpline(sketch, "E253", {"points": [v(-2.7, -9.28) * mm, v(-2.72, -9.38) * mm, v(-2.74, -9.47) * mm, v(-2.75, -9.55) * mm]});
            skFitSpline(sketch, "E254", {"points": [v(-2.75, -9.55) * mm, v(-2.76, -9.63) * mm, v(-2.77, -9.7) * mm, v(-2.77, -9.76) * mm]});
            skFitSpline(sketch, "E255", {"points": [v(-2.77, -9.76) * mm, v(-2.77, -9.92) * mm, v(-2.72, -10) * mm, v(-2.62, -10) * mm]});
            skLineSegment(sketch, "E256", {"start": v(-2.62, -10) * mm, "end": v(-2.1, -10) * mm});
            skFitSpline(sketch, "E257", {"points": [v(-2.1, -10) * mm, v(-2, -10) * mm, v(-1.93, -9.94) * mm, v(-1.88, -9.82) * mm]});
            skFitSpline(sketch, "E258", {"points": [v(-1.88, -9.82) * mm, v(-1.82, -9.7) * mm, v(-1.76, -9.52) * mm, v(-1.7, -9.28) * mm]});
            skFitSpline(sketch, "E259", {"points": [v(6.85, -5.57) * mm, v(6.87, -5.51) * mm, v(6.88, -5.4) * mm, v(6.88, -5.24) * mm]});
            skFitSpline(sketch, "E260", {"points": [v(6.88, -5.24) * mm, v(6.88, -5.12) * mm, v(6.87, -5) * mm, v(6.84, -4.87) * mm]});
            skFitSpline(sketch, "E261", {"points": [v(6.84, -4.87) * mm, v(6.82, -4.74) * mm, v(6.78, -4.62) * mm, v(6.74, -4.52) * mm]});
            skFitSpline(sketch, "E262", {"points": [v(6.74, -4.52) * mm, v(6.7, -4.42) * mm, v(6.64, -4.34) * mm, v(6.58, -4.28) * mm]});
            skFitSpline(sketch, "E263", {"points": [v(6.58, -4.28) * mm, v(6.52, -4.21) * mm, v(6.44, -4.18) * mm, v(6.36, -4.18) * mm]});
            skLineSegment(sketch, "E264", {"start": v(6.36, -4.18) * mm, "end": v(4.5, -4.18) * mm});
            skFitSpline(sketch, "E265", {"points": [v(4.5, -4.18) * mm, v(4.4, -4.18) * mm, v(4.3, -4.23) * mm, v(4.18, -4.33) * mm]});
            skFitSpline(sketch, "E266", {"points": [v(4.18, -4.33) * mm, v(4.06, -4.42) * mm, v(3.95, -4.53) * mm, v(3.85, -4.67) * mm]});
            skFitSpline(sketch, "E267", {"points": [v(3.85, -4.67) * mm, v(3.74, -4.81) * mm, v(3.65, -4.96) * mm, v(3.57, -5.12) * mm]});
            skFitSpline(sketch, "E268", {"points": [v(3.57, -5.12) * mm, v(3.5, -5.29) * mm, v(3.44, -5.44) * mm, v(3.4, -5.57) * mm]});
            skLineSegment(sketch, "E269", {"start": v(3.4, -5.57) * mm, "end": v(2.77, -8.6) * mm});
            skFitSpline(sketch, "E270", {"points": [v(2.77, -8.6) * mm, v(2.74, -8.69) * mm, v(2.73, -8.8) * mm, v(2.73, -8.94) * mm]});
            skFitSpline(sketch, "E271", {"points": [v(2.73, -8.94) * mm, v(2.73, -9.07) * mm, v(2.74, -9.2) * mm, v(2.77, -9.32) * mm]});
            skFitSpline(sketch, "E272", {"points": [v(2.77, -9.32) * mm, v(2.8, -9.44) * mm, v(2.82, -9.56) * mm, v(2.87, -9.66) * mm]});
            skFitSpline(sketch, "E273", {"points": [v(2.87, -9.66) * mm, v(2.91, -9.76) * mm, v(2.97, -9.84) * mm, v(3.03, -9.9) * mm]});
            skFitSpline(sketch, "E274", {"points": [v(3.03, -9.9) * mm, v(3.1, -9.97) * mm, v(3.17, -10) * mm, v(3.25, -10) * mm]});
            skLineSegment(sketch, "E275", {"start": v(3.25, -10) * mm, "end": v(5.12, -10) * mm});
            skFitSpline(sketch, "E276", {"points": [v(5.12, -10) * mm, v(5.22, -10) * mm, v(5.33, -9.95) * mm, v(5.44, -9.86) * mm]});
            skFitSpline(sketch, "E277", {"points": [v(5.44, -9.86) * mm, v(5.55, -9.77) * mm, v(5.66, -9.65) * mm, v(5.76, -9.52) * mm]});
            skFitSpline(sketch, "E278", {"points": [v(5.76, -9.52) * mm, v(5.87, -9.37) * mm, v(5.96, -9.22) * mm, v(6.04, -9.06) * mm]});
            skFitSpline(sketch, "E279", {"points": [v(6.04, -9.06) * mm, v(6.12, -8.9) * mm, v(6.17, -8.74) * mm, v(6.2, -8.6) * mm]});
            skLineSegment(sketch, "E280", {"start": v(6.2, -8.6) * mm, "end": v(6.85, -5.57) * mm});
            skFitSpline(sketch, "E281", {"points": [v(5.51, -5.64) * mm, v(5.58, -5.64) * mm, v(5.64, -5.67) * mm, v(5.69, -5.73) * mm]});
            skFitSpline(sketch, "E282", {"points": [v(5.69, -5.73) * mm, v(5.74, -5.78) * mm, v(5.76, -5.87) * mm, v(5.76, -5.99) * mm]});
            skLineSegment(sketch, "E283", {"start": v(5.76, -5.99) * mm, "end": v(5.76, -6.02) * mm});
            skLineSegment(sketch, "E284", {"start": v(5.76, -6.02) * mm, "end": v(5.3, -8.16) * mm});
            skFitSpline(sketch, "E285", {"points": [v(5.3, -8.16) * mm, v(5.26, -8.28) * mm, v(5.2, -8.38) * mm, v(5.12, -8.45) * mm]});
            skFitSpline(sketch, "E286", {"points": [v(5.12, -8.45) * mm, v(5.05, -8.5) * mm, v(4.98, -8.54) * mm, v(4.91, -8.54) * mm]});
            skLineSegment(sketch, "E287", {"start": v(4.91, -8.54) * mm, "end": v(4.1, -8.54) * mm});
            skFitSpline(sketch, "E288", {"points": [v(4.1, -8.54) * mm, v(4.03, -8.54) * mm, v(3.97, -8.51) * mm, v(3.92, -8.46) * mm]});
            skFitSpline(sketch, "E289", {"points": [v(3.92, -8.46) * mm, v(3.87, -8.4) * mm, v(3.85, -8.31) * mm, v(3.85, -8.2) * mm]});
            skLineSegment(sketch, "E290", {"start": v(3.85, -8.2) * mm, "end": v(3.85, -8.16) * mm});
            skLineSegment(sketch, "E291", {"start": v(3.85, -8.16) * mm, "end": v(4.3, -6.02) * mm});
            skFitSpline(sketch, "E292", {"points": [v(4.3, -6.02) * mm, v(4.35, -5.9) * mm, v(4.42, -5.8) * mm, v(4.5, -5.73) * mm]});
            skFitSpline(sketch, "E293", {"points": [v(4.5, -5.73) * mm, v(4.58, -5.67) * mm, v(4.65, -5.64) * mm, v(4.71, -5.64) * mm]});
            skLineSegment(sketch, "E294", {"start": v(4.71, -5.64) * mm, "end": v(5.51, -5.64) * mm});
            skLineSegment(sketch, "E295", {"start": v(9.93, -8.6) * mm, "end": v(10.66, -5.2) * mm});
            skFitSpline(sketch, "E296", {"points": [v(10.66, -5.2) * mm, v(10.7, -5.04) * mm, v(10.71, -4.88) * mm, v(10.71, -4.73) * mm]});
            skFitSpline(sketch, "E297", {"points": [v(10.71, -4.73) * mm, v(10.71, -4.57) * mm, v(10.7, -4.45) * mm, v(10.65, -4.34) * mm]});
            skFitSpline(sketch, "E298", {"points": [v(10.65, -4.34) * mm, v(10.61, -4.24) * mm, v(10.55, -4.18) * mm, v(10.46, -4.18) * mm]});
            skLineSegment(sketch, "E299", {"start": v(10.46, -4.18) * mm, "end": v(7.86, -4.18) * mm});
            skFitSpline(sketch, "E300", {"points": [v(7.86, -4.18) * mm, v(7.77, -4.18) * mm, v(7.7, -4.24) * mm, v(7.64, -4.35) * mm]});
            skFitSpline(sketch, "E301", {"points": [v(7.64, -4.35) * mm, v(7.59, -4.46) * mm, v(7.53, -4.64) * mm, v(7.48, -4.9) * mm]});
            skLineSegment(sketch, "E302", {"start": v(7.48, -4.9) * mm, "end": v(6.54, -9.28) * mm});
            skFitSpline(sketch, "E303", {"points": [v(6.54, -9.28) * mm, v(6.52, -9.38) * mm, v(6.5, -9.47) * mm, v(6.49, -9.55) * mm]});
            skFitSpline(sketch, "E304", {"points": [v(6.49, -9.55) * mm, v(6.48, -9.63) * mm, v(6.47, -9.7) * mm, v(6.47, -9.76) * mm]});
            skFitSpline(sketch, "E305", {"points": [v(6.47, -9.76) * mm, v(6.47, -9.92) * mm, v(6.52, -10) * mm, v(6.62, -10) * mm]});
            skLineSegment(sketch, "E306", {"start": v(6.62, -10) * mm, "end": v(8.85, -10) * mm});
            skFitSpline(sketch, "E307", {"points": [v(8.85, -10) * mm, v(8.95, -10) * mm, v(9.05, -9.95) * mm, v(9.17, -9.86) * mm]});
            skFitSpline(sketch, "E308", {"points": [v(9.17, -9.86) * mm, v(9.28, -9.77) * mm, v(9.4, -9.65) * mm, v(9.5, -9.52) * mm]});
            skFitSpline(sketch, "E309", {"points": [v(9.5, -9.52) * mm, v(9.6, -9.37) * mm, v(9.69, -9.22) * mm, v(9.76, -9.06) * mm]});
            skFitSpline(sketch, "E310", {"points": [v(9.76, -9.06) * mm, v(9.85, -8.9) * mm, v(9.9, -8.74) * mm, v(9.93, -8.6) * mm]});
            skFitSpline(sketch, "E311", {"points": [v(9.45, -5.64) * mm, v(9.5, -5.64) * mm, v(9.52, -5.69) * mm, v(9.52, -5.79) * mm]});
            skFitSpline(sketch, "E312", {"points": [v(9.52, -5.79) * mm, v(9.52, -5.83) * mm, v(9.52, -5.88) * mm, v(9.5, -5.95) * mm]});
            skFitSpline(sketch, "E313", {"points": [v(9.5, -5.95) * mm, v(9.5, -6) * mm, v(9.49, -6.05) * mm, v(9.48, -6.1) * mm]});
            skLineSegment(sketch, "E314", {"start": v(9.48, -6.1) * mm, "end": v(9.04, -8.16) * mm});
            skFitSpline(sketch, "E315", {"points": [v(9.04, -8.16) * mm, v(8.99, -8.29) * mm, v(8.92, -8.38) * mm, v(8.84, -8.45) * mm]});
            skFitSpline(sketch, "E316", {"points": [v(8.84, -8.45) * mm, v(8.77, -8.5) * mm, v(8.7, -8.54) * mm, v(8.63, -8.54) * mm]});
            skLineSegment(sketch, "E317", {"start": v(8.63, -8.54) * mm, "end": v(7.78, -8.54) * mm});
            skFitSpline(sketch, "E318", {"points": [v(7.78, -8.54) * mm, v(7.76, -8.54) * mm, v(7.75, -8.53) * mm, v(7.74, -8.5) * mm]});
            skFitSpline(sketch, "E319", {"points": [v(7.74, -8.5) * mm, v(7.73, -8.47) * mm, v(7.73, -8.44) * mm, v(7.73, -8.4) * mm]});
            skFitSpline(sketch, "E320", {"points": [v(7.73, -8.4) * mm, v(7.73, -8.4) * mm, v(7.73, -8.38) * mm, v(7.73, -8.36) * mm]});
            skFitSpline(sketch, "E321", {"points": [v(7.73, -8.36) * mm, v(7.73, -8.35) * mm, v(7.74, -8.32) * mm, v(7.74, -8.3) * mm]});
            skLineSegment(sketch, "E322", {"start": v(7.74, -8.3) * mm, "end": v(8.25, -5.89) * mm});
            skFitSpline(sketch, "E323", {"points": [v(8.25, -5.89) * mm, v(8.27, -5.83) * mm, v(8.29, -5.78) * mm, v(8.31, -5.73) * mm]});
            skFitSpline(sketch, "E324", {"points": [v(8.31, -5.73) * mm, v(8.34, -5.67) * mm, v(8.37, -5.64) * mm, v(8.4, -5.64) * mm]});
            skLineSegment(sketch, "E325", {"start": v(8.4, -5.64) * mm, "end": v(9.45, -5.64) * mm});
            skLineSegment(sketch, "E326", {"start": v(13.65, -8.6) * mm, "end": v(14.38, -5.2) * mm});
            skFitSpline(sketch, "E327", {"points": [v(14.38, -5.2) * mm, v(14.42, -5.04) * mm, v(14.44, -4.88) * mm, v(14.44, -4.73) * mm]});
            skFitSpline(sketch, "E328", {"points": [v(14.44, -4.73) * mm, v(14.44, -4.57) * mm, v(14.42, -4.45) * mm, v(14.37, -4.34) * mm]});
            skFitSpline(sketch, "E329", {"points": [v(14.37, -4.34) * mm, v(14.33, -4.24) * mm, v(14.27, -4.18) * mm, v(14.18, -4.18) * mm]});
            skLineSegment(sketch, "E330", {"start": v(14.18, -4.18) * mm, "end": v(11.59, -4.18) * mm});
            skFitSpline(sketch, "E331", {"points": [v(11.59, -4.18) * mm, v(11.5, -4.18) * mm, v(11.42, -4.24) * mm, v(11.36, -4.35) * mm]});
            skFitSpline(sketch, "E332", {"points": [v(11.36, -4.35) * mm, v(11.3, -4.46) * mm, v(11.25, -4.64) * mm, v(11.2, -4.9) * mm]});
            skLineSegment(sketch, "E333", {"start": v(11.2, -4.9) * mm, "end": v(10.27, -9.28) * mm});
            skFitSpline(sketch, "E334", {"points": [v(10.27, -9.28) * mm, v(10.25, -9.38) * mm, v(10.23, -9.47) * mm, v(10.21, -9.55) * mm]});
            skFitSpline(sketch, "E335", {"points": [v(10.21, -9.55) * mm, v(10.2, -9.63) * mm, v(10.2, -9.7) * mm, v(10.2, -9.76) * mm]});
            skFitSpline(sketch, "E336", {"points": [v(10.2, -9.76) * mm, v(10.2, -9.92) * mm, v(10.24, -10) * mm, v(10.34, -10) * mm]});
            skLineSegment(sketch, "E337", {"start": v(10.34, -10) * mm, "end": v(12.57, -10) * mm});
            skFitSpline(sketch, "E338", {"points": [v(12.57, -10) * mm, v(12.67, -10) * mm, v(12.78, -9.95) * mm, v(12.9, -9.86) * mm]});
            skFitSpline(sketch, "E339", {"points": [v(12.9, -9.86) * mm, v(13, -9.77) * mm, v(13.11, -9.65) * mm, v(13.22, -9.52) * mm]});
            skFitSpline(sketch, "E340", {"points": [v(13.22, -9.52) * mm, v(13.32, -9.37) * mm, v(13.4, -9.22) * mm, v(13.49, -9.06) * mm]});
            skFitSpline(sketch, "E341", {"points": [v(13.49, -9.06) * mm, v(13.57, -8.9) * mm, v(13.62, -8.74) * mm, v(13.65, -8.6) * mm]});
            skFitSpline(sketch, "E342", {"points": [v(13.17, -5.64) * mm, v(13.22, -5.64) * mm, v(13.25, -5.69) * mm, v(13.25, -5.79) * mm]});
            skFitSpline(sketch, "E343", {"points": [v(13.25, -5.79) * mm, v(13.25, -5.83) * mm, v(13.24, -5.88) * mm, v(13.23, -5.95) * mm]});
            skFitSpline(sketch, "E344", {"points": [v(13.23, -5.95) * mm, v(13.22, -6) * mm, v(13.21, -6.05) * mm, v(13.2, -6.1) * mm]});
            skLineSegment(sketch, "E345", {"start": v(13.2, -6.1) * mm, "end": v(12.76, -8.16) * mm});
            skFitSpline(sketch, "E346", {"points": [v(12.76, -8.16) * mm, v(12.71, -8.29) * mm, v(12.65, -8.38) * mm, v(12.57, -8.45) * mm]});
            skFitSpline(sketch, "E347", {"points": [v(12.57, -8.45) * mm, v(12.49, -8.5) * mm, v(12.42, -8.54) * mm, v(12.35, -8.54) * mm]});
            skLineSegment(sketch, "E348", {"start": v(12.35, -8.54) * mm, "end": v(11.5, -8.54) * mm});
            skFitSpline(sketch, "E349", {"points": [v(11.5, -8.54) * mm, v(11.48, -8.54) * mm, v(11.47, -8.53) * mm, v(11.46, -8.5) * mm]});
            skFitSpline(sketch, "E350", {"points": [v(11.46, -8.5) * mm, v(11.46, -8.47) * mm, v(11.45, -8.44) * mm, v(11.45, -8.4) * mm]});
            skFitSpline(sketch, "E351", {"points": [v(11.45, -8.4) * mm, v(11.45, -8.4) * mm, v(11.45, -8.38) * mm, v(11.45, -8.36) * mm]});
            skFitSpline(sketch, "E352", {"points": [v(11.45, -8.36) * mm, v(11.46, -8.35) * mm, v(11.46, -8.32) * mm, v(11.46, -8.3) * mm]});
            skLineSegment(sketch, "E353", {"start": v(11.46, -8.3) * mm, "end": v(11.98, -5.89) * mm});
            skFitSpline(sketch, "E354", {"points": [v(11.98, -5.89) * mm, v(11.99, -5.83) * mm, v(12, -5.78) * mm, v(12.04, -5.73) * mm]});
            skFitSpline(sketch, "E355", {"points": [v(12.04, -5.73) * mm, v(12.07, -5.67) * mm, v(12.1, -5.64) * mm, v(12.12, -5.64) * mm]});
            skLineSegment(sketch, "E356", {"start": v(12.12, -5.64) * mm, "end": v(13.17, -5.64) * mm});
            skFitSpline(sketch, "E357", {"points": [v(14.13, -8.6) * mm, v(14.1, -8.69) * mm, v(14.1, -8.8) * mm, v(14.1, -8.94) * mm]});
            skFitSpline(sketch, "E358", {"points": [v(14.1, -8.94) * mm, v(14.1, -9.07) * mm, v(14.1, -9.2) * mm, v(14.13, -9.32) * mm]});
            skFitSpline(sketch, "E359", {"points": [v(14.13, -9.32) * mm, v(14.15, -9.44) * mm, v(14.19, -9.56) * mm, v(14.23, -9.66) * mm]});
            skFitSpline(sketch, "E360", {"points": [v(14.23, -9.66) * mm, v(14.28, -9.76) * mm, v(14.33, -9.84) * mm, v(14.4, -9.9) * mm]});
            skFitSpline(sketch, "E361", {"points": [v(14.4, -9.9) * mm, v(14.46, -9.97) * mm, v(14.53, -10) * mm, v(14.61, -10) * mm]});
            skLineSegment(sketch, "E362", {"start": v(14.61, -10) * mm, "end": v(16.52, -10) * mm});
            skFitSpline(sketch, "E363", {"points": [v(16.52, -10) * mm, v(16.6, -10) * mm, v(16.67, -9.98) * mm, v(16.75, -9.94) * mm]});
            skFitSpline(sketch, "E364", {"points": [v(16.75, -9.94) * mm, v(16.83, -9.9) * mm, v(16.9, -9.83) * mm, v(16.97, -9.75) * mm]});
            skFitSpline(sketch, "E365", {"points": [v(16.97, -9.75) * mm, v(17.03, -9.67) * mm, v(17.1, -9.58) * mm, v(17.14, -9.47) * mm]});
            skFitSpline(sketch, "E366", {"points": [v(17.14, -9.47) * mm, v(17.2, -9.36) * mm, v(17.24, -9.24) * mm, v(17.27, -9.1) * mm]});
            skFitSpline(sketch, "E367", {"points": [v(17.27, -9.1) * mm, v(17.28, -9.07) * mm, v(17.28, -9.02) * mm, v(17.3, -8.93) * mm]});
            skFitSpline(sketch, "E368", {"points": [v(17.3, -8.93) * mm, v(17.3, -8.84) * mm, v(17.3, -8.76) * mm, v(17.3, -8.68) * mm]});
            skFitSpline(sketch, "E369", {"points": [v(17.3, -8.68) * mm, v(17.3, -8.59) * mm, v(17.3, -8.54) * mm, v(17.27, -8.54) * mm]});
            skLineSegment(sketch, "E370", {"start": v(17.27, -8.54) * mm, "end": v(15.44, -8.54) * mm});
            skFitSpline(sketch, "E371", {"points": [v(15.44, -8.54) * mm, v(15.38, -8.54) * mm, v(15.33, -8.52) * mm, v(15.27, -8.47) * mm]});
            skFitSpline(sketch, "E372", {"points": [v(15.27, -8.47) * mm, v(15.22, -8.43) * mm, v(15.2, -8.35) * mm, v(15.2, -8.25) * mm]});
            skFitSpline(sketch, "E373", {"points": [v(15.2, -8.25) * mm, v(15.2, -8.25) * mm, v(15.2, -8.24) * mm, v(15.2, -8.23) * mm]});
            skFitSpline(sketch, "E374", {"points": [v(15.2, -8.23) * mm, v(15.2, -8.2) * mm, v(15.2, -8.19) * mm, v(15.2, -8.16) * mm]});
            skFitSpline(sketch, "E375", {"points": [v(15.2, -8.16) * mm, v(15.24, -8.05) * mm, v(15.27, -7.96) * mm, v(15.3, -7.91) * mm]});
            skFitSpline(sketch, "E376", {"points": [v(15.3, -7.91) * mm, v(15.33, -7.86) * mm, v(15.36, -7.83) * mm, v(15.4, -7.83) * mm]});
            skLineSegment(sketch, "E377", {"start": v(15.4, -7.83) * mm, "end": v(16.9, -7.83) * mm});
            skFitSpline(sketch, "E378", {"points": [v(16.9, -7.83) * mm, v(16.94, -7.83) * mm, v(16.98, -7.8) * mm, v(17.03, -7.74) * mm]});
            skFitSpline(sketch, "E379", {"points": [v(17.03, -7.74) * mm, v(17.07, -7.67) * mm, v(17.12, -7.6) * mm, v(17.16, -7.5) * mm]});
            skFitSpline(sketch, "E380", {"points": [v(17.16, -7.5) * mm, v(17.2, -7.4) * mm, v(17.24, -7.3) * mm, v(17.28, -7.18) * mm]});
            skFitSpline(sketch, "E381", {"points": [v(17.28, -7.18) * mm, v(17.32, -7.07) * mm, v(17.34, -6.96) * mm, v(17.37, -6.86) * mm]});
            skFitSpline(sketch, "E382", {"points": [v(17.37, -6.86) * mm, v(17.38, -6.83) * mm, v(17.39, -6.77) * mm, v(17.4, -6.7) * mm]});
            skFitSpline(sketch, "E383", {"points": [v(17.4, -6.7) * mm, v(17.4, -6.6) * mm, v(17.42, -6.53) * mm, v(17.42, -6.47) * mm]});
            skFitSpline(sketch, "E384", {"points": [v(17.42, -6.47) * mm, v(17.42, -6.4) * mm, v(17.4, -6.35) * mm, v(17.38, -6.35) * mm]});
            skLineSegment(sketch, "E385", {"start": v(17.38, -6.35) * mm, "end": v(15.69, -6.35) * mm});
            skFitSpline(sketch, "E386", {"points": [v(15.69, -6.35) * mm, v(15.67, -6.35) * mm, v(15.65, -6.34) * mm, v(15.65, -6.31) * mm]});
            skFitSpline(sketch, "E387", {"points": [v(15.65, -6.31) * mm, v(15.64, -6.28) * mm, v(15.63, -6.25) * mm, v(15.63, -6.22) * mm]});
            skFitSpline(sketch, "E388", {"points": [v(15.63, -6.22) * mm, v(15.63, -6.2) * mm, v(15.63, -6.2) * mm, v(15.63, -6.18) * mm]});
            skFitSpline(sketch, "E389", {"points": [v(15.63, -6.18) * mm, v(15.64, -6.16) * mm, v(15.64, -6.14) * mm, v(15.65, -6.1) * mm]});
            skFitSpline(sketch, "E390", {"points": [v(15.65, -6.1) * mm, v(15.65, -6.06) * mm, v(15.66, -6.01) * mm, v(15.68, -5.96) * mm]});
            skFitSpline(sketch, "E391", {"points": [v(15.68, -5.96) * mm, v(15.7, -5.9) * mm, v(15.7, -5.86) * mm, v(15.73, -5.81) * mm]});
            skFitSpline(sketch, "E392", {"points": [v(15.73, -5.81) * mm, v(15.75, -5.76) * mm, v(15.77, -5.72) * mm, v(15.8, -5.7) * mm]});
            skFitSpline(sketch, "E393", {"points": [v(15.8, -5.7) * mm, v(15.82, -5.66) * mm, v(15.84, -5.64) * mm, v(15.87, -5.64) * mm]});
            skLineSegment(sketch, "E394", {"start": v(15.87, -5.64) * mm, "end": v(17.73, -5.64) * mm});
            skFitSpline(sketch, "E395", {"points": [v(17.73, -5.64) * mm, v(17.78, -5.64) * mm, v(17.82, -5.61) * mm, v(17.87, -5.56) * mm]});
            skFitSpline(sketch, "E396", {"points": [v(17.87, -5.56) * mm, v(17.92, -5.5) * mm, v(17.96, -5.42) * mm, v(18, -5.33) * mm]});
            skFitSpline(sketch, "E397", {"points": [v(18, -5.33) * mm, v(18.05, -5.23) * mm, v(18.09, -5.13) * mm, v(18.12, -5.01) * mm]});
            skFitSpline(sketch, "E398", {"points": [v(18.12, -5.01) * mm, v(18.16, -4.9) * mm, v(18.2, -4.8) * mm, v(18.22, -4.7) * mm]});
            skFitSpline(sketch, "E399", {"points": [v(18.22, -4.7) * mm, v(18.23, -4.66) * mm, v(18.24, -4.6) * mm, v(18.25, -4.52) * mm]});
            skFitSpline(sketch, "E400", {"points": [v(18.25, -4.52) * mm, v(18.26, -4.44) * mm, v(18.27, -4.36) * mm, v(18.27, -4.3) * mm]});
            skFitSpline(sketch, "E401", {"points": [v(18.27, -4.3) * mm, v(18.27, -4.22) * mm, v(18.25, -4.18) * mm, v(18.22, -4.18) * mm]});
            skLineSegment(sketch, "E402", {"start": v(18.22, -4.18) * mm, "end": v(15.49, -4.18) * mm});
            skFitSpline(sketch, "E403", {"points": [v(15.49, -4.18) * mm, v(15.42, -4.18) * mm, v(15.35, -4.21) * mm, v(15.3, -4.28) * mm]});
            skFitSpline(sketch, "E404", {"points": [v(15.3, -4.28) * mm, v(15.23, -4.33) * mm, v(15.17, -4.4) * mm, v(15.11, -4.5) * mm]});
            skFitSpline(sketch, "E405", {"points": [v(15.11, -4.5) * mm, v(15.06, -4.6) * mm, v(15, -4.71) * mm, v(14.96, -4.84) * mm]});
            skFitSpline(sketch, "E406", {"points": [v(14.96, -4.84) * mm, v(14.92, -4.96) * mm, v(14.88, -5.08) * mm, v(14.86, -5.2) * mm]});
            skLineSegment(sketch, "E407", {"start": v(14.86, -5.2) * mm, "end": v(14.13, -8.6) * mm});
            skLineSegment(sketch, "E408", {"start": v(14.13, -8.6) * mm, "end": v(14.13, -8.6) * mm});
            skLineSegment(sketch, "E409", {"start": v(21.1, -8.6) * mm, "end": v(21.83, -5.2) * mm});
            skFitSpline(sketch, "E410", {"points": [v(21.83, -5.2) * mm, v(21.87, -5.04) * mm, v(21.9, -4.88) * mm, v(21.9, -4.73) * mm]});
            skFitSpline(sketch, "E411", {"points": [v(21.9, -4.73) * mm, v(21.9, -4.57) * mm, v(21.87, -4.45) * mm, v(21.83, -4.34) * mm]});
            skFitSpline(sketch, "E412", {"points": [v(21.83, -4.34) * mm, v(21.79, -4.24) * mm, v(21.73, -4.18) * mm, v(21.64, -4.18) * mm]});
            skLineSegment(sketch, "E413", {"start": v(21.64, -4.18) * mm, "end": v(19.04, -4.18) * mm});
            skFitSpline(sketch, "E414", {"points": [v(19.04, -4.18) * mm, v(18.95, -4.18) * mm, v(18.88, -4.24) * mm, v(18.82, -4.35) * mm]});
            skFitSpline(sketch, "E415", {"points": [v(18.82, -4.35) * mm, v(18.76, -4.46) * mm, v(18.7, -4.64) * mm, v(18.65, -4.9) * mm]});
            skLineSegment(sketch, "E416", {"start": v(18.65, -4.9) * mm, "end": v(17.72, -9.28) * mm});
            skFitSpline(sketch, "E417", {"points": [v(17.72, -9.28) * mm, v(17.7, -9.38) * mm, v(17.68, -9.47) * mm, v(17.67, -9.55) * mm]});
            skFitSpline(sketch, "E418", {"points": [v(17.67, -9.55) * mm, v(17.66, -9.63) * mm, v(17.65, -9.7) * mm, v(17.65, -9.76) * mm]});
            skFitSpline(sketch, "E419", {"points": [v(17.65, -9.76) * mm, v(17.65, -9.92) * mm, v(17.7, -10) * mm, v(17.8, -10) * mm]});
            skLineSegment(sketch, "E420", {"start": v(17.8, -10) * mm, "end": v(20.03, -10) * mm});
            skFitSpline(sketch, "E421", {"points": [v(20.03, -10) * mm, v(20.13, -10) * mm, v(20.23, -9.95) * mm, v(20.35, -9.86) * mm]});
            skFitSpline(sketch, "E422", {"points": [v(20.35, -9.86) * mm, v(20.46, -9.77) * mm, v(20.57, -9.65) * mm, v(20.67, -9.52) * mm]});
            skFitSpline(sketch, "E423", {"points": [v(20.67, -9.52) * mm, v(20.77, -9.37) * mm, v(20.86, -9.22) * mm, v(20.94, -9.06) * mm]});
            skFitSpline(sketch, "E424", {"points": [v(20.94, -9.06) * mm, v(21.03, -8.9) * mm, v(21.08, -8.74) * mm, v(21.1, -8.6) * mm]});
            skFitSpline(sketch, "E425", {"points": [v(20.63, -5.64) * mm, v(20.68, -5.64) * mm, v(20.7, -5.69) * mm, v(20.7, -5.79) * mm]});
            skFitSpline(sketch, "E426", {"points": [v(20.7, -5.79) * mm, v(20.7, -5.83) * mm, v(20.7, -5.88) * mm, v(20.68, -5.95) * mm]});
            skFitSpline(sketch, "E427", {"points": [v(20.68, -5.95) * mm, v(20.68, -6) * mm, v(20.67, -6.05) * mm, v(20.66, -6.1) * mm]});
            skLineSegment(sketch, "E428", {"start": v(20.66, -6.1) * mm, "end": v(20.22, -8.16) * mm});
            skFitSpline(sketch, "E429", {"points": [v(20.22, -8.16) * mm, v(20.17, -8.29) * mm, v(20.1, -8.38) * mm, v(20.02, -8.45) * mm]});
            skFitSpline(sketch, "E430", {"points": [v(20.02, -8.45) * mm, v(19.94, -8.5) * mm, v(19.87, -8.54) * mm, v(19.8, -8.54) * mm]});
            skLineSegment(sketch, "E431", {"start": v(19.8, -8.54) * mm, "end": v(18.96, -8.54) * mm});
            skFitSpline(sketch, "E432", {"points": [v(18.96, -8.54) * mm, v(18.94, -8.54) * mm, v(18.93, -8.53) * mm, v(18.92, -8.5) * mm]});
            skFitSpline(sketch, "E433", {"points": [v(18.92, -8.5) * mm, v(18.91, -8.47) * mm, v(18.9, -8.44) * mm, v(18.9, -8.4) * mm]});
            skFitSpline(sketch, "E434", {"points": [v(18.9, -8.4) * mm, v(18.9, -8.4) * mm, v(18.9, -8.38) * mm, v(18.9, -8.36) * mm]});
            skFitSpline(sketch, "E435", {"points": [v(18.9, -8.36) * mm, v(18.91, -8.35) * mm, v(18.92, -8.32) * mm, v(18.92, -8.3) * mm]});
            skLineSegment(sketch, "E436", {"start": v(18.92, -8.3) * mm, "end": v(19.43, -5.89) * mm});
            skFitSpline(sketch, "E437", {"points": [v(19.43, -5.89) * mm, v(19.44, -5.83) * mm, v(19.46, -5.78) * mm, v(19.5, -5.73) * mm]});
            skFitSpline(sketch, "E438", {"points": [v(19.5, -5.73) * mm, v(19.52, -5.67) * mm, v(19.55, -5.64) * mm, v(19.58, -5.64) * mm]});
            skLineSegment(sketch, "E439", {"start": v(19.58, -5.64) * mm, "end": v(20.63, -5.64) * mm});
            skLineSegment(sketch, "E440", {"start": v(-25.13, 0.05) * mm, "end": v(25.12, 0.05) * mm, "construction": true});
            skLineSegment(sketch, "E441", {"start": v(25.12, 0.05) * mm, "end": v(25.12, -14.45) * mm, "construction": true});
            skLineSegment(sketch, "E442", {"start": v(25.12, -14.45) * mm, "end": v(-25.13, -14.45) * mm, "construction": true});
            skLineSegment(sketch, "E443", {"start": v(-25.13, -14.45) * mm, "end": v(-25.13, 0.05) * mm, "construction": true});
            skSolve(sketch);
        }
        {
            var Q0;
            Q0=makeQuery(id+"F0.imprint","IMPRINT",FACE,{"disambiguationData":[TD([[makeQuery(id+"F0.imprint","IMPRINT",EDGE,{"derivedFrom":sQuery(id+"F0.wireOp",EDGE,"E0.bottom")}),-1.0]])]});
            extrude(context, id + "F2", {"entities" : qUnion([Q0]), "depth" : 0.3 * mm});
        }
        {
            var Q0;
            Q0=makeQuery(id+"F1.imprint","IMPRINT",FACE,{"disambiguationData":[TD([[makeQuery(id+"F1.imprint","IMPRINT",EDGE,{"derivedFrom":sQuery(id+"F1.wireOp",EDGE,"E5")}),1.0]])]});
            var Q1;
            Q1=makeQuery(id+"F1.imprint","IMPRINT",FACE,{"disambiguationData":[TD([[makeQuery(id+"F1.imprint","IMPRINT",EDGE,{"derivedFrom":sQuery(id+"F1.wireOp",EDGE,"E49")}),1.0]])]});
            var Q2;
            Q2=makeQuery(id+"F1.imprint","IMPRINT",FACE,{"disambiguationData":[TD([[makeQuery(id+"F1.imprint","IMPRINT",EDGE,{"derivedFrom":sQuery(id+"F1.wireOp",EDGE,"E100")}),1.0]])]});
            var Q3;
            Q3=makeQuery(id+"F1.imprint","IMPRINT",FACE,{"disambiguationData":[TD([[makeQuery(id+"F1.imprint","IMPRINT",EDGE,{"derivedFrom":sQuery(id+"F1.wireOp",EDGE,"E132")}),-1.0]])]});
            var Q4;
            Q4=makeQuery(id+"F1.imprint","IMPRINT",FACE,{"disambiguationData":[TD([[makeQuery(id+"F1.imprint","IMPRINT",EDGE,{"derivedFrom":sQuery(id+"F1.wireOp",EDGE,"E176")}),1.0]])]});
            var Q5;
            Q5=makeQuery(id+"F1.imprint","IMPRINT",FACE,{"disambiguationData":[TD([[makeQuery(id+"F1.imprint","IMPRINT",EDGE,{"derivedFrom":sQuery(id+"F1.wireOp",EDGE,"E212")}),1.0]])]});
            var Q6;
            Q6=makeQuery(id+"F1.imprint","IMPRINT",FACE,{"disambiguationData":[TD([[makeQuery(id+"F1.imprint","IMPRINT",EDGE,{"derivedFrom":sQuery(id+"F1.wireOp",EDGE,"E259")}),1.0]])]});
            var Q7;
            Q7=makeQuery(id+"F1.imprint","IMPRINT",FACE,{"disambiguationData":[TD([[makeQuery(id+"F1.imprint","IMPRINT",EDGE,{"derivedFrom":sQuery(id+"F1.wireOp",EDGE,"E295")}),1.0]])]});
            var Q8;
            Q8=makeQuery(id+"F1.imprint","IMPRINT",FACE,{"disambiguationData":[TD([[makeQuery(id+"F1.imprint","IMPRINT",EDGE,{"derivedFrom":sQuery(id+"F1.wireOp",EDGE,"E326")}),1.0]])]});
            var Q9;
            Q9=makeQuery(id+"F1.imprint","IMPRINT",FACE,{"disambiguationData":[TD([[makeQuery(id+"F1.imprint","IMPRINT",EDGE,{"derivedFrom":sQuery(id+"F1.wireOp",EDGE,"E357")}),1.0]])]});
            var Q10;
            Q10=makeQuery(id+"F1.imprint","IMPRINT",FACE,{"disambiguationData":[TD([[makeQuery(id+"F1.imprint","IMPRINT",EDGE,{"derivedFrom":sQuery(id+"F1.wireOp",EDGE,"E409")}),1.0]])]});
            extrude(context, id + "F3", {"entities" : qUnion([Q0, Q1, Q2, Q3, Q4, Q5, Q6, Q7, Q8, Q9, Q10]), "operationType" : NewBodyOperationType.ADD, "depth" : (0.3 + 0.3) * mm});
        }
    });
